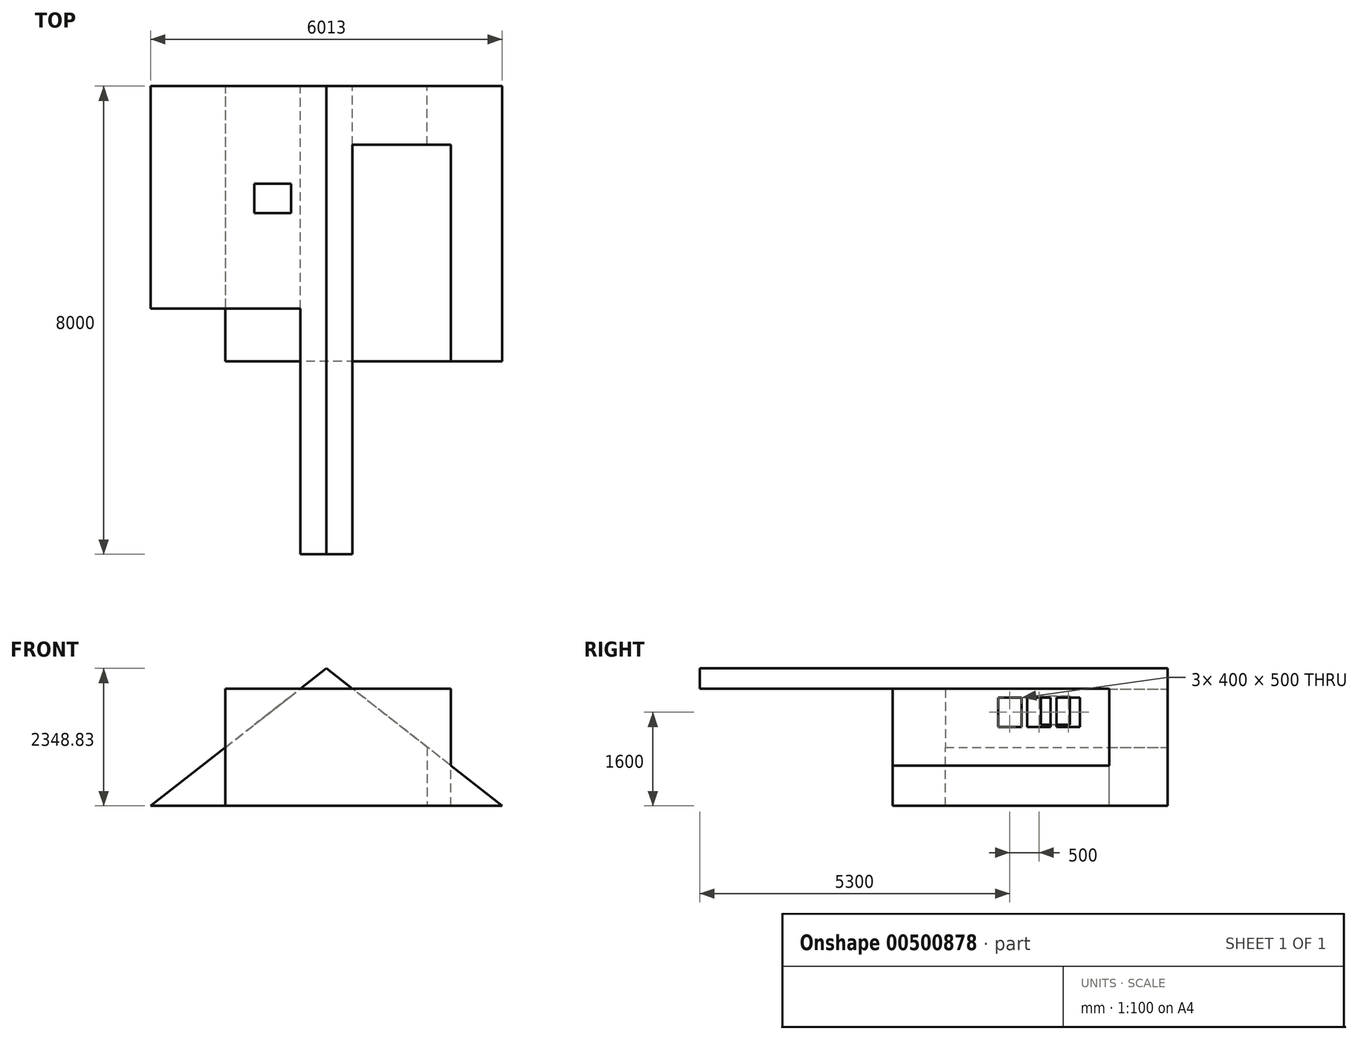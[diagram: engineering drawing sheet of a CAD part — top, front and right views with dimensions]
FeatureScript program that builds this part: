
annotation { "Feature Type Name" : "Feature", "Feature Type Description" : "" }
export const myFeature = defineFeature(function(context is Context, id is Id, definition is map)
    precondition{}
    {
        {
            var Q0;
            Q0=qCreatedBy(makeId("Top.planeOp"),FACE);
            var sketch = newSketch(context, id + "F0", { "sketchPlane" : qUnion([Q0])});
            skLineSegment(sketch, "E0.bottom", {"start": v(0, 0) * mm, "end": v(3453, 0) * mm});
            skLineSegment(sketch, "E0.top", {"start": v(0, 4701) * mm, "end": v(3453, 4701) * mm});
            skLineSegment(sketch, "E0.left", {"start": v(0, 0) * mm, "end": v(0, 4701) * mm});
            skLineSegment(sketch, "E0.right", {"start": v(3453, 0) * mm, "end": v(3453, 4701) * mm});
            skSolve(sketch);
        }
        {
            var Q0;
            Q0 = qSketchRegion(id + "F0", true);
            extrude(context, id + "F1", {"entities" : qUnion([Q0]), "depth" : 2000 * mm, "offsetDistance" : 25 * mm});
        }
        {
            var Q0;
            Q0=makeQuery(id+"F1.opExtrude","SWEPT_FACE",FACE,{"disambiguationData":[OSD([sQuery(id+"F0.wireOp",EDGE,"E0.top")])]});
            var sketch = newSketch(context, id + "F2", { "sketchPlane" : qUnion([Q0])});
            skLineSegment(sketch, "E1", {"start": v(-3453, 1000) * mm, "end": v(-2173, 2000) * mm});
            skLineSegment(sketch, "E2", {"start": v(-2173, 2000) * mm, "end": v(-3453, 2000) * mm});
            skLineSegment(sketch, "E3", {"start": v(-3453, 2000) * mm, "end": v(-3453, 1000) * mm});
            skSolve(sketch);
        }
        {
            var Q0;
            Q0 = qSketchRegion(id + "F2", true);
            extrude(context, id + "F3", {"entities" : qUnion([Q0]), "operationType" : NewBodyOperationType.REMOVE, "oppositeDirection" : true, "depth" : 1000 * mm, "offsetDistance" : 25 * mm});
        }
        {
            var Q0;
            Q0=makeQuery(id+"F1.opExtrude","SWEPT_FACE",FACE,{"disambiguationData":[OSD([sQuery(id+"F0.wireOp",EDGE,"E0.top")])]});
            var sketch = newSketch(context, id + "F4", { "sketchPlane" : qUnion([Q0])});
            skLineSegment(sketch, "E4", {"start": v(0, 1000) * mm, "end": v(-1280, 2000) * mm});
            skLineSegment(sketch, "E5", {"start": v(-1280, 2000) * mm, "end": v(0, 2000) * mm});
            skLineSegment(sketch, "E6", {"start": v(0, 2000) * mm, "end": v(0, 1000) * mm});
            skSolve(sketch);
        }
        {
            var Q0;
            Q0 = qSketchRegion(id + "F4", true);
            extrude(context, id + "F5", {"entities" : qUnion([Q0]), "operationType" : NewBodyOperationType.REMOVE, "oppositeDirection" : true, "depth" : 3800 * mm, "offsetDistance" : 25 * mm});
        }
        {
            var Q0;
            Q0=makeQuery(id+"F3.boolean.opBoolean","COPY",FACE,{"derivedFrom":makeQuery(id+"F3.opExtrude","CAP_FACE",FACE,{"disambiguationData":[OSD([sQuery(id+"F2.wireOp",EDGE,"E1"),sQuery(id+"F2.wireOp",EDGE,"E2"),sQuery(id+"F2.wireOp",EDGE,"E3")])],"isStart":false})});
            var sketch = newSketch(context, id + "F6", { "sketchPlane" : qUnion([Q0])});
            skLineSegment(sketch, "E7", {"start": v(-2173, 2000) * mm, "end": v(-2173, 2000) * mm});
            skLineSegment(sketch, "E8", {"start": v(-3453, 2000) * mm, "end": v(-3853, 2000) * mm});
            skLineSegment(sketch, "E9", {"start": v(-3853, 2000) * mm, "end": v(-3853, 0) * mm});
            skLineSegment(sketch, "E10", {"start": v(-3453, 2000) * mm, "end": v(-3453, 0) * mm});
            skLineSegment(sketch, "E11", {"start": v(-3453, 0) * mm, "end": v(-3853, 0) * mm});
            skSolve(sketch);
        }
        {
            var Q0;
            Q0 = qSketchRegion(id + "F6", true);
            var Q1;
            Q1=makeQuery(id+"F1.opExtrude","SWEPT_FACE",FACE,{"disambiguationData":[OSD([sQuery(id+"F0.wireOp",EDGE,"E0.bottom")])]});
            extrude(context, id + "F7", {"entities" : qUnion([Q0]), "operationType" : NewBodyOperationType.ADD, "endBound" : BoundingType.UP_TO_SURFACE, "oppositeDirection" : true, "depth" : 25 * mm, "endBoundEntityFace" : qUnion([Q1]), "offsetDistance" : 25 * mm});
        }
        {
            var Q0;
            Q0=makeQuery(id+"F1.opExtrude","CAP_FACE",FACE,{"disambiguationData":[OSD([sQuery(id+"F0.wireOp",EDGE,"E0.bottom"),sQuery(id+"F0.wireOp",EDGE,"E0.top"),sQuery(id+"F0.wireOp",EDGE,"E0.left"),sQuery(id+"F0.wireOp",EDGE,"E0.right")])],"isStart":true});
            shell(context, id + "F8", {"entities" : qUnion([Q0]), "thickness" : 2.5 * mm});
        }
        {
            var Q0;
            Q0=makeQuery(id+"F7.opExtrude","SWEPT_FACE",FACE,{"disambiguationData":[OSD([sQuery(id+"F6.wireOp",EDGE,"E9")])]});
            var sketch = newSketch(context, id + "F9", { "sketchPlane" : qUnion([Q0])});
            skLineSegment(sketch, "E12.bottom", {"start": v(3201, 1850) * mm, "end": v(2801, 1850) * mm});
            skLineSegment(sketch, "E12.top", {"start": v(3201, 1350) * mm, "end": v(2801, 1350) * mm});
            skLineSegment(sketch, "E12.left", {"start": v(3201, 1850) * mm, "end": v(3201, 1350) * mm});
            skLineSegment(sketch, "E12.right", {"start": v(2801, 1850) * mm, "end": v(2801, 1350) * mm});
            skLineSegment(sketch, "E13.bottom", {"start": v(2701, 1850) * mm, "end": v(2301, 1850) * mm});
            skLineSegment(sketch, "E13.top", {"start": v(2701, 1350) * mm, "end": v(2301, 1350) * mm});
            skLineSegment(sketch, "E13.left", {"start": v(2701, 1850) * mm, "end": v(2701, 1350) * mm});
            skLineSegment(sketch, "E13.right", {"start": v(2301, 1850) * mm, "end": v(2301, 1350) * mm});
            skLineSegment(sketch, "E14.bottom", {"start": v(2201, 1850) * mm, "end": v(1801, 1850) * mm});
            skLineSegment(sketch, "E14.top", {"start": v(2201, 1350) * mm, "end": v(1801, 1350) * mm});
            skLineSegment(sketch, "E14.left", {"start": v(2201, 1850) * mm, "end": v(2201, 1350) * mm});
            skLineSegment(sketch, "E14.right", {"start": v(1801, 1850) * mm, "end": v(1801, 1350) * mm});
            skSolve(sketch);
        }
        {
            var Q0;
            Q0 = qSketchRegion(id + "F9", true);
            extrude(context, id + "F10", {"entities" : qUnion([Q0]), "operationType" : NewBodyOperationType.REMOVE, "endBound" : BoundingType.UP_TO_NEXT, "oppositeDirection" : true, "depth" : 25 * mm, "offsetDistance" : 25 * mm});
        }
        {
            var Q0;
            Q0=makeQuery(id+"F5.boolean.opBoolean","COPY",FACE,{"derivedFrom":makeQuery(id+"F5.opExtrude","SWEPT_FACE",FACE,{"disambiguationData":[OSD([sQuery(id+"F4.wireOp",EDGE,"E4")])]})});
            var sketch = newSketch(context, id + "F11", { "sketchPlane" : qUnion([Q0])});
            skLineSegment(sketch, "E15.bottom", {"start": v(2039.96, 3032.24) * mm, "end": v(1239.96, 3032.24) * mm});
            skLineSegment(sketch, "E15.top", {"start": v(2039.96, 2532.24) * mm, "end": v(1239.96, 2532.24) * mm});
            skLineSegment(sketch, "E15.left", {"start": v(2039.96, 3032.24) * mm, "end": v(2039.96, 2532.24) * mm});
            skLineSegment(sketch, "E15.right", {"start": v(1239.96, 3032.24) * mm, "end": v(1239.96, 2532.24) * mm});
            skSolve(sketch);
        }
        {
            var Q0;
            Q0 = qSketchRegion(id + "F11", true);
            extrude(context, id + "F12", {"entities" : qUnion([Q0]), "operationType" : NewBodyOperationType.REMOVE, "endBound" : BoundingType.UP_TO_NEXT, "oppositeDirection" : true, "depth" : 25 * mm, "offsetDistance" : 25 * mm});
        }
        {
            var Q0;
            Q0=makeQuery(id+"F7.boolean.opBoolean","MERGE",FACE,{"derivedFrom":[makeQuery(id+"F3.boolean.opBoolean","COPY",FACE,{"derivedFrom":makeQuery(id+"F3.opExtrude","CAP_FACE",FACE,{"disambiguationData":[OSD([sQuery(id+"F2.wireOp",EDGE,"E1"),sQuery(id+"F2.wireOp",EDGE,"E2"),sQuery(id+"F2.wireOp",EDGE,"E3")])],"isStart":false})}),makeQuery(id+"F7.opExtrude","CAP_FACE",FACE,{"disambiguationData":[OSD([sQuery(id+"F6.wireOp",EDGE,"E8"),sQuery(id+"F6.wireOp",EDGE,"E9"),sQuery(id+"F6.wireOp",EDGE,"E10"),sQuery(id+"F6.wireOp",EDGE,"E11")])],"isStart":true})]});
            var sketch = newSketch(context, id + "F13", { "sketchPlane" : qUnion([Q0])});
            skLineSegment(sketch, "E16", {"start": v(-3453, 1000) * mm, "end": v(-4733, 0) * mm});
            skLineSegment(sketch, "E17", {"start": v(-4733, 0) * mm, "end": v(-3453, 0) * mm});
            skLineSegment(sketch, "E18", {"start": v(-3453, 0) * mm, "end": v(-3453, 1000) * mm});
            skSolve(sketch);
        }
        {
            var Q0;
            Q0 = qSketchRegion(id + "F13", true);
            var Q1;
            Q1=makeQuery(id+"F1.opExtrude","SWEPT_FACE",FACE,{"disambiguationData":[OSD([sQuery(id+"F0.wireOp",EDGE,"E0.top")])]});
            extrude(context, id + "F14", {"entities" : qUnion([Q0]), "operationType" : NewBodyOperationType.ADD, "endBound" : BoundingType.UP_TO_SURFACE, "depth" : 25 * mm, "endBoundEntityFace" : qUnion([Q1]), "offsetDistance" : 25 * mm});
        }
        {
            var Q0;
            Q0=makeQuery(id+"F14.opExtrude","CAP_FACE",FACE,{"disambiguationData":[OSD([sQuery(id+"F13.wireOp",EDGE,"E16"),sQuery(id+"F13.wireOp",EDGE,"E17"),sQuery(id+"F13.wireOp",EDGE,"E18")])],"isStart":true});
            var sketch = newSketch(context, id + "F15", { "sketchPlane" : qUnion([Q0])});
            skLineSegment(sketch, "E19", {"start": v(3853, 687.5) * mm, "end": v(4733, 0) * mm});
            skLineSegment(sketch, "E20", {"start": v(4733, 0) * mm, "end": v(3853, 0) * mm});
            skLineSegment(sketch, "E21", {"start": v(3853, 0) * mm, "end": v(3853, 687.5) * mm});
            skSolve(sketch);
        }
        {
            var Q0;
            Q0 = qSketchRegion(id + "F15", true);
            var Q1;
            Q1=makeQuery(id+"F7.boolean.opBoolean","MERGE",FACE,{"derivedFrom":[makeQuery(id+"F1.opExtrude","SWEPT_FACE",FACE,{"disambiguationData":[OSD([sQuery(id+"F0.wireOp",EDGE,"E0.bottom")])]}),makeQuery(id+"F7.opExtrude","CAP_FACE",FACE,{"disambiguationData":[OSD([sQuery(id+"F6.wireOp",EDGE,"E8"),sQuery(id+"F6.wireOp",EDGE,"E9"),sQuery(id+"F6.wireOp",EDGE,"E10"),sQuery(id+"F6.wireOp",EDGE,"E11")])],"isStart":false})]});
            extrude(context, id + "F16", {"entities" : qUnion([Q0]), "operationType" : NewBodyOperationType.ADD, "endBound" : BoundingType.UP_TO_SURFACE, "depth" : 25 * mm, "endBoundEntityFace" : qUnion([Q1]), "offsetDistance" : 25 * mm});
        }
        {
            var Q0;
            Q0=makeQuery(id+"F14.boolean.opBoolean","MERGE",FACE,{"derivedFrom":[makeQuery(id+"F1.opExtrude","SWEPT_FACE",FACE,{"disambiguationData":[OSD([sQuery(id+"F0.wireOp",EDGE,"E0.top")])]}),makeQuery(id+"F14.opExtrude","CAP_FACE",FACE,{"disambiguationData":[OSD([sQuery(id+"F13.wireOp",EDGE,"E16"),sQuery(id+"F13.wireOp",EDGE,"E17"),sQuery(id+"F13.wireOp",EDGE,"E18")])],"isStart":false})]});
            var sketch = newSketch(context, id + "F17", { "sketchPlane" : qUnion([Q0])});
            skLineSegment(sketch, "E22", {"start": v(0, 1000) * mm, "end": v(1280, 0) * mm});
            skLineSegment(sketch, "E23", {"start": v(1280, 0) * mm, "end": v(0, 0) * mm});
            skLineSegment(sketch, "E24", {"start": v(0, 0) * mm, "end": v(0, 1000) * mm});
            skSolve(sketch);
        }
        {
            var Q0;
            Q0 = qSketchRegion(id + "F17", true);
            var Q1;
            Q1=makeQuery(id+"F5.boolean.opBoolean","COPY",FACE,{"derivedFrom":makeQuery(id+"F5.opExtrude","CAP_FACE",FACE,{"disambiguationData":[OSD([sQuery(id+"F4.wireOp",EDGE,"E4"),sQuery(id+"F4.wireOp",EDGE,"E5"),sQuery(id+"F4.wireOp",EDGE,"E6")])],"isStart":false})});
            extrude(context, id + "F18", {"entities" : qUnion([Q0]), "operationType" : NewBodyOperationType.ADD, "endBound" : BoundingType.UP_TO_SURFACE, "oppositeDirection" : true, "depth" : 25 * mm, "endBoundEntityFace" : qUnion([Q1]), "offsetDistance" : 25 * mm});
        }
        {
            var Q0;
            Q0=makeQuery(id+"F18.boolean.opBoolean","MERGE",FACE,{"derivedFrom":[makeQuery(id+"F14.boolean.opBoolean","MERGE",FACE,{"derivedFrom":[makeQuery(id+"F1.opExtrude","SWEPT_FACE",FACE,{"disambiguationData":[OSD([sQuery(id+"F0.wireOp",EDGE,"E0.top")])]}),makeQuery(id+"F14.opExtrude","CAP_FACE",FACE,{"disambiguationData":[OSD([sQuery(id+"F13.wireOp",EDGE,"E16"),sQuery(id+"F13.wireOp",EDGE,"E17"),sQuery(id+"F13.wireOp",EDGE,"E18")])],"isStart":false})]}),makeQuery(id+"F18.opExtrude","CAP_FACE",FACE,{"disambiguationData":[OSD([sQuery(id+"F17.wireOp",EDGE,"E22"),sQuery(id+"F17.wireOp",EDGE,"E23"),sQuery(id+"F17.wireOp",EDGE,"E24")])],"isStart":true})]});
            var sketch = newSketch(context, id + "F19", { "sketchPlane" : qUnion([Q0])});
            skLineSegment(sketch, "E25", {"start": v(-1280, 2000) * mm, "end": v(-2173, 2000) * mm});
            skLineSegment(sketch, "E26", {"start": v(-2173, 2000) * mm, "end": v(-1726.5, 2348.83) * mm});
            skLineSegment(sketch, "E27", {"start": v(-1280, 2000) * mm, "end": v(-1726.5, 2348.83) * mm});
            skSolve(sketch);
        }
        {
            var Q0;
            Q0 = qSketchRegion(id + "F19", true);
            var Q1;
            Q1=makeQuery(id+"F16.boolean.opBoolean","MERGE",FACE,{"derivedFrom":[makeQuery(id+"F7.boolean.opBoolean","MERGE",FACE,{"derivedFrom":[makeQuery(id+"F1.opExtrude","SWEPT_FACE",FACE,{"disambiguationData":[OSD([sQuery(id+"F0.wireOp",EDGE,"E0.bottom")])]}),makeQuery(id+"F7.opExtrude","CAP_FACE",FACE,{"disambiguationData":[OSD([sQuery(id+"F6.wireOp",EDGE,"E8"),sQuery(id+"F6.wireOp",EDGE,"E9"),sQuery(id+"F6.wireOp",EDGE,"E10"),sQuery(id+"F6.wireOp",EDGE,"E11")])],"isStart":false})]}),makeQuery(id+"F16.opExtrude","CAP_FACE",FACE,{"disambiguationData":[OSD([sQuery(id+"F15.wireOp",EDGE,"E19"),sQuery(id+"F15.wireOp",EDGE,"E20"),sQuery(id+"F15.wireOp",EDGE,"E21")])],"isStart":false})]});
            extrude(context, id + "F20", {"entities" : qUnion([Q0]), "operationType" : NewBodyOperationType.ADD, "oppositeDirection" : true, "depth" : 8000 * mm, "endBoundEntityFace" : qUnion([Q1]), "offsetDistance" : 25 * mm});
        }
    });
